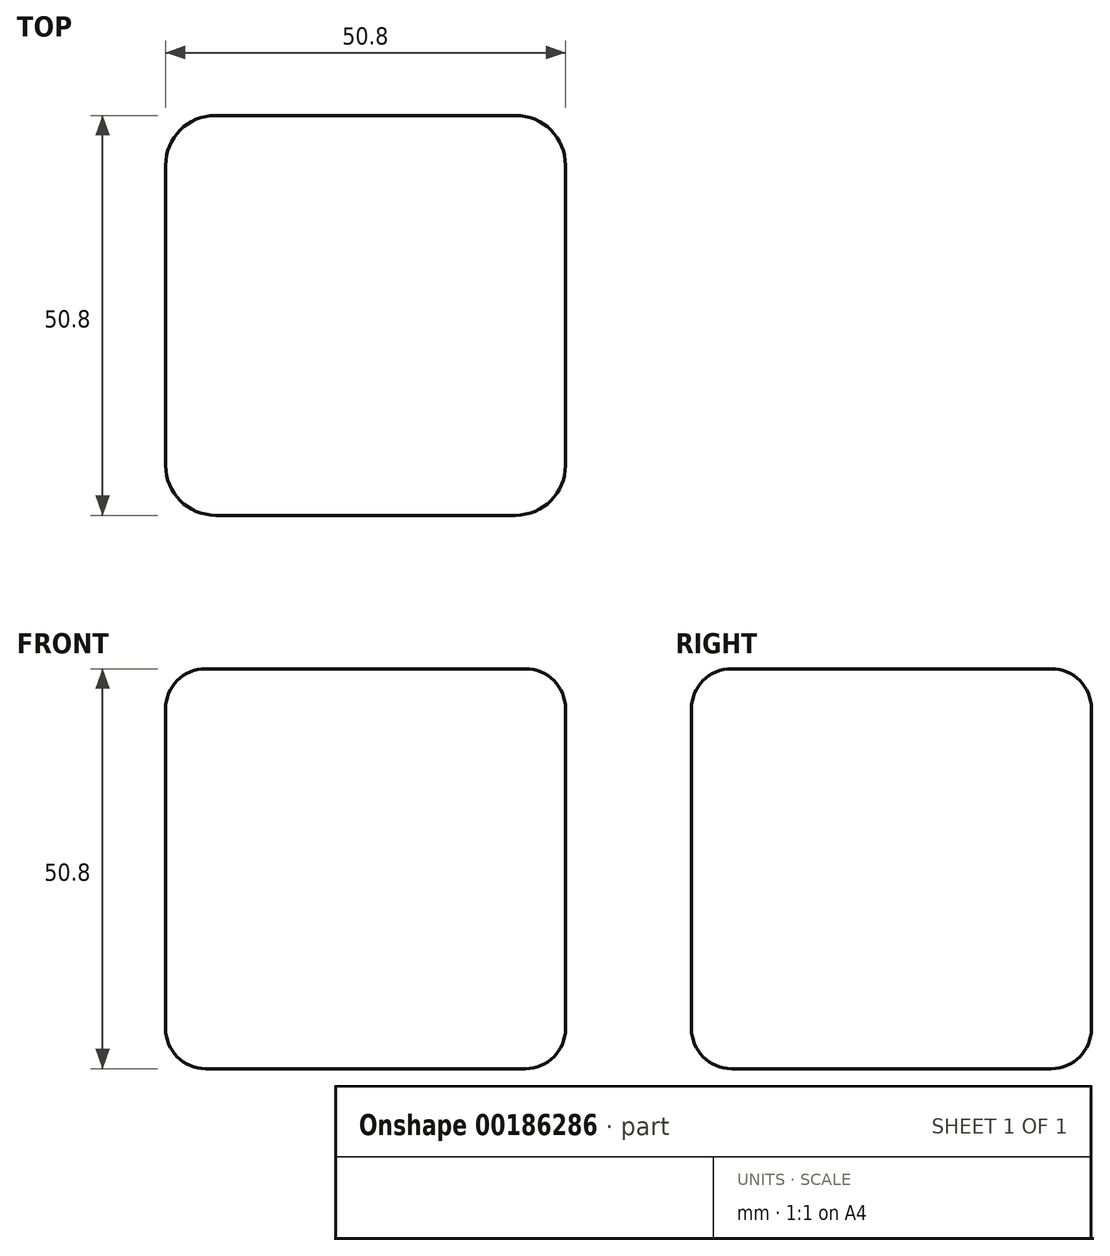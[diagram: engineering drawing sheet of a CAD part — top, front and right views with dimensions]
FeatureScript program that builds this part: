
annotation { "Feature Type Name" : "Feature", "Feature Type Description" : "" }
export const myFeature = defineFeature(function(context is Context, id is Id, definition is map)
    precondition{}
    {
        {
            var Q0;
            Q0=qCreatedBy(makeId("Top.planeOp"),FACE);
            var sketch = newSketch(context, id + "F0", { "sketchPlane" : qUnion([Q0])});
            skLineSegment(sketch, "E0.bottom", {"start": v(19.05, -25.4) * mm, "end": v(-19.05, -25.4) * mm});
            skLineSegment(sketch, "E0.top", {"start": v(19.05, 25.4) * mm, "end": v(-19.05, 25.4) * mm});
            skLineSegment(sketch, "E0.left", {"start": v(25.4, -19.05) * mm, "end": v(25.4, 19.05) * mm});
            skLineSegment(sketch, "E0.right", {"start": v(-25.4, -19.05) * mm, "end": v(-25.4, 19.05) * mm});
            skPoint(sketch, "E0.middle", {"position": v(0, 0) * mm});
            skPoint(sketch, "E1.visualSharp", {"position": v(25.4, 25.4) * mm});
            skArc(sketch, "E1.filletArc", {"start": v(25.4, 19.05) * mm, "mid": v(23.54, 23.54) * mm, "end": v(19.05, 25.4) * mm});
            skPoint(sketch, "E2.visualSharp", {"position": v(25.4, -25.4) * mm});
            skArc(sketch, "E2.filletArc", {"start": v(19.05, -25.4) * mm, "mid": v(23.54, -23.54) * mm, "end": v(25.4, -19.05) * mm});
            skPoint(sketch, "E3.visualSharp", {"position": v(-25.4, -25.4) * mm});
            skArc(sketch, "E3.filletArc", {"start": v(-25.4, -19.05) * mm, "mid": v(-23.54, -23.54) * mm, "end": v(-19.05, -25.4) * mm});
            skPoint(sketch, "E4.visualSharp", {"position": v(-25.4, 25.4) * mm});
            skArc(sketch, "E4.filletArc", {"start": v(-19.05, 25.4) * mm, "mid": v(-23.54, 23.54) * mm, "end": v(-25.4, 19.05) * mm});
            skSolve(sketch);
        }
        {
            var Q0;
            Q0 = qSketchRegion(id + "F0", true);
            extrude(context, id + "F1", {"entities" : qUnion([Q0]), "depth" : 50.8 * mm});
        }
        {
            var Q0;
            Q0=makeQuery(id+"F1.opExtrude","CAP_EDGE",EDGE,{"disambiguationData":[OSD([sQuery(id+"F0.wireOp",EDGE,"E0.left")])],"isStart":true});
            fillet(context, id + "F2", {"entities" : qUnion([Q0]), "radius" : 5.08 * mm, "tangentPropagation" : true, "allowEdgeOverflow" : false});
        }
        {
            var Q0;
            Q0=makeQuery(id+"F1.opExtrude","CAP_EDGE",EDGE,{"disambiguationData":[OSD([sQuery(id+"F0.wireOp",EDGE,"E0.left")])],"isStart":false});
            fillet(context, id + "F3", {"entities" : qUnion([Q0]), "radius" : 5.08 * mm, "tangentPropagation" : true, "allowEdgeOverflow" : false});
        }
    });
